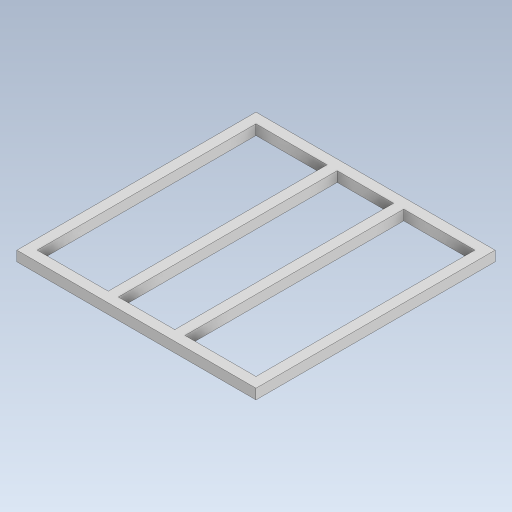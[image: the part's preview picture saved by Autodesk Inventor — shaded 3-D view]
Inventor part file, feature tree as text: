
AUTODESK INVENTOR PART (.ipt)
format: ipt  version: 2023 (Build 270158000, 158)  size: 111,616 bytes
history: native  units: in
note: dims shown in document units (in); Inventor stores cm internally (conversion verified against a paired STEP export)
features: extrude x1, sketch x1
ambient origin geometry x8: Origin, YZ Plane, XZ Plane, XY Plane, X Axis, Y Axis, Z Axis, Center Point
bodies: Solid1 (feature_tree)
feature tree (2):
  extrude  "Extrusion1"  Depth=23.622in
  sketch  "Sketch1"  dims[d0=23.622in d1=23.622in d2=1.0in d3=1.0in d4=15.6in d5=1.0in d6=0.0in]
